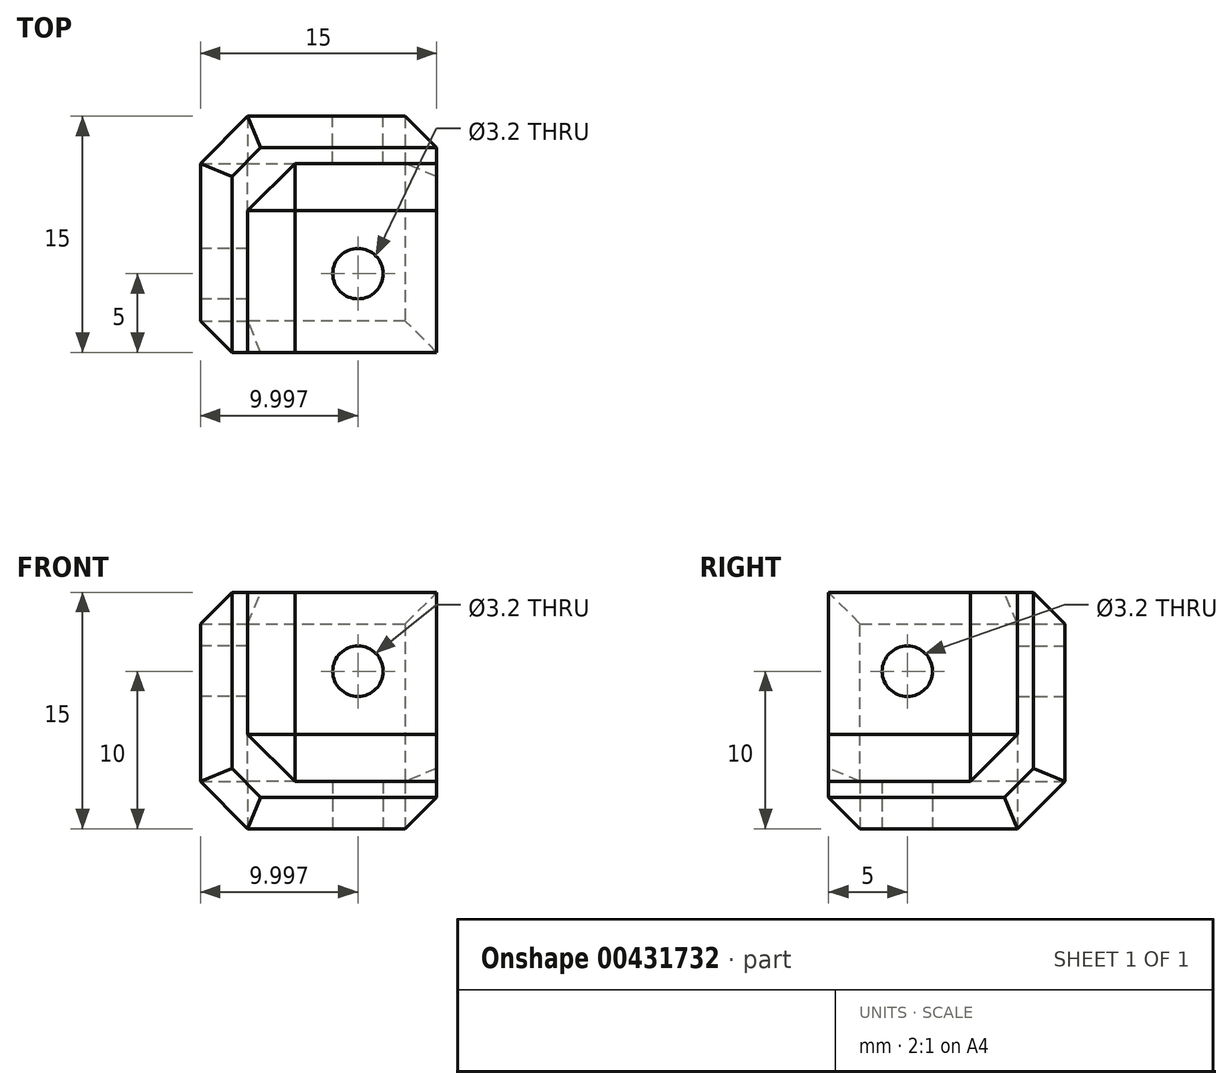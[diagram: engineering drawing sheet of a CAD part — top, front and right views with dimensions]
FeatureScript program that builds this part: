
annotation { "Feature Type Name" : "Feature", "Feature Type Description" : "" }
export const myFeature = defineFeature(function(context is Context, id is Id, definition is map)
    precondition{}
    {
        {
            var Q0;
            Q0=qCreatedBy(makeId("Top.planeOp"),FACE);
            var sketch = newSketch(context, id + "F0", { "sketchPlane" : qUnion([Q0])});
            skLineSegment(sketch, "E0.bottom", {"start": v(-55.5, 0.14) * mm, "end": v(-40.5, 0.14) * mm});
            skLineSegment(sketch, "E0.top", {"start": v(-55.5, -14.86) * mm, "end": v(-40.5, -14.86) * mm});
            skLineSegment(sketch, "E0.left", {"start": v(-55.5, 0.14) * mm, "end": v(-55.5, -14.86) * mm});
            skLineSegment(sketch, "E0.right", {"start": v(-40.5, 0.14) * mm, "end": v(-40.5, -14.86) * mm});
            skLineSegment(sketch, "E1", {"start": v(-52.5, -14.86) * mm, "end": v(-52.5, -2.86) * mm});
            skLineSegment(sketch, "E2", {"start": v(-52.5, -2.86) * mm, "end": v(-40.5, -2.86) * mm});
            skCircle(sketch, "E3", {"center": v(-45.5, -9.86) * mm, "radius": 1.6 * mm});
            skSolve(sketch);
        }
        {
            var Q0;
            {var subQ1=sQuery(id+"F0.wireOp",EDGE,"E0.bottom");Q0=makeQuery(id+"F0.imprint","IMPRINT",FACE,{"disambiguationData":[TD([[makeQuery(id+"F0.imprint","IMPRINT",EDGE,{"derivedFrom":subQ1}),-1.0]])]});}
            var Q1;
            {var subQ3=sQuery(id+"F0.wireOp",EDGE,"E1");Q1=makeQuery(id+"F0.imprint","IMPRINT",FACE,{"disambiguationData":[TD([[makeQuery(id+"F0.imprint","IMPRINT",EDGE,{"derivedFrom":subQ3}),-1.0]])]});}
            extrude(context, id + "F1", {"entities" : qUnion([Q0, Q1]), "depth" : 3 * mm});
        }
        {
            var Q0;
            {var subQ1=sQuery(id+"F0.wireOp",EDGE,"E0.bottom");Q0=makeQuery(id+"F0.imprint","IMPRINT",FACE,{"disambiguationData":[TD([[makeQuery(id+"F0.imprint","IMPRINT",EDGE,{"derivedFrom":subQ1}),-1.0]])]});}
            extrude(context, id + "F2", {"entities" : qUnion([Q0]), "operationType" : NewBodyOperationType.ADD, "depth" : 15 * mm});
        }
        {
            var Q0;
            {var subQ0=sQuery(id+"F0.wireOp",EDGE,"E0.bottom");Q0=makeQuery(id+"F2.boolean.opBoolean","MERGE",FACE,{"derivedFrom":[makeQuery(id+"F1.opExtrude","SWEPT_FACE",FACE,{"disambiguationData":[OSD([subQ0])]}),makeQuery(id+"F2.opExtrude","SWEPT_FACE",FACE,{"disambiguationData":[OSD([subQ0])]})]});}
            var sketch = newSketch(context, id + "F3", { "sketchPlane" : qUnion([Q0])});
            skCircle(sketch, "E4", {"center": v(45.5, 10) * mm, "radius": 1.6 * mm});
            skSolve(sketch);
        }
        {
            var Q0;
            Q0=qSketchRegion(id+"F3",true);
            extrude(context, id + "F4", {"entities" : qUnion([Q0]), "operationType" : NewBodyOperationType.REMOVE, "oppositeDirection" : true, "depth" : 25 * mm});
        }
        {
            var Q0;
            {var subQ0=sQuery(id+"F0.wireOp",EDGE,"E0.left");Q0=makeQuery(id+"F2.boolean.opBoolean","MERGE",FACE,{"derivedFrom":[makeQuery(id+"F1.opExtrude","SWEPT_FACE",FACE,{"disambiguationData":[OSD([subQ0])]}),makeQuery(id+"F2.opExtrude","SWEPT_FACE",FACE,{"disambiguationData":[OSD([subQ0])]})]});}
            var sketch = newSketch(context, id + "F5", { "sketchPlane" : qUnion([Q0])});
            skCircle(sketch, "E5", {"center": v(9.86, 10) * mm, "radius": 1.6 * mm});
            skSolve(sketch);
        }
        {
            var Q0;
            Q0=qSketchRegion(id+"F5",true);
            extrude(context, id + "F6", {"entities" : qUnion([Q0]), "operationType" : NewBodyOperationType.REMOVE, "oppositeDirection" : true, "depth" : 25 * mm});
        }
        {
            var Q0;
            Q0=makeQuery(id+"F2.opExtrude","CAP_VERTEX",VERTEX,{"disambiguationData":[OSD([sQuery(id+"F0.wireOp",EDGE,"E0.top"),sQuery(id+"F0.wireOp",EDGE,"E1")])],"isStart":false});
            var Q1;
            Q1=makeQuery(id+"F2.opExtrude","CAP_VERTEX",VERTEX,{"disambiguationData":[OSD([sQuery(id+"F0.wireOp",EDGE,"E0.right"),sQuery(id+"F0.wireOp",EDGE,"E2")])],"isStart":false});
            var Q2;
            Q2=makeQuery(id+"F1.opExtrude","CAP_VERTEX",VERTEX,{"disambiguationData":[OSD([sQuery(id+"F0.wireOp",EDGE,"E0.top"),sQuery(id+"F0.wireOp",EDGE,"E0.right")])],"isStart":false});
            cPlane(context, id + "F7", {"entities" : qUnion([Q0, Q1, Q2]), "cplaneType" : CPlaneType.THREE_POINT, "offset" : 25 * mm, "width" : 150 * mm, "height" : 150 * mm});
        }
        {
            var Q0;
            Q0=qCreatedBy(id+"F7.planeOp",FACE);
            var sketch = newSketch(context, id + "F8", { "sketchPlane" : qUnion([Q0])});
            skLineSegment(sketch, "E6", {"start": v(-30.2, 50.45) * mm, "end": v(-13.73, 49.44) * mm});
            skLineSegment(sketch, "E7", {"start": v(-13.73, 49.44) * mm, "end": v(-6.86, 39.33) * mm});
            skLineSegment(sketch, "E8", {"start": v(-6.86, 39.33) * mm, "end": v(-16.3, 24.65) * mm});
            skLineSegment(sketch, "E9", {"start": v(-16.3, 24.65) * mm, "end": v(-31.74, 25.37) * mm});
            skLineSegment(sketch, "E10", {"start": v(-31.74, 25.37) * mm, "end": v(-37.56, 38.88) * mm});
            skLineSegment(sketch, "E11", {"start": v(-37.56, 38.88) * mm, "end": v(-30.2, 50.45) * mm});
            skSolve(sketch);
        }
        {
            var Q0;
            Q0=qSketchRegion(id+"F8",true);
            extrude(context, id + "F9", {"entities" : qUnion([Q0]), "operationType" : NewBodyOperationType.REMOVE, "oppositeDirection" : true, "depth" : 3 * mm});
        }
        {
            var Q0;
            Q0=makeQuery(id+"F1.opExtrude","CAP_EDGE",EDGE,{"disambiguationData":[OSD([sQuery(id+"F0.wireOp",EDGE,"E0.left")])],"isStart":true});
            var Q1;
            Q1=makeQuery(id+"F1.opExtrude","CAP_EDGE",EDGE,{"disambiguationData":[OSD([sQuery(id+"F0.wireOp",EDGE,"E0.bottom")])],"isStart":true});
            var Q2;
            {var subQ0=sQuery(id+"F0.wireOp",EDGE,"E0.left");var subQ1=sQuery(id+"F0.wireOp",EDGE,"E0.bottom");Q2=makeQuery(id+"F2.boolean.opBoolean","MERGE",EDGE,{"derivedFrom":[makeQuery(id+"F1.opExtrude","SWEPT_EDGE",EDGE,{"disambiguationData":[OSD([subQ1,subQ0])]}),makeQuery(id+"F2.opExtrude","SWEPT_EDGE",EDGE,{"disambiguationData":[OSD([subQ1,subQ0])]})]});}
            var Q3;
            Q3=makeQuery(id+"F2.boolean.opBoolean","INTERSECT",EDGE,{"derivedFrom":[makeQuery(id+"F1.opExtrude","CAP_FACE",FACE,{"disambiguationData":[OSD([sQuery(id+"F0.wireOp",EDGE,"E0.bottom"),sQuery(id+"F0.wireOp",EDGE,"E0.top"),sQuery(id+"F0.wireOp",EDGE,"E0.left"),sQuery(id+"F0.wireOp",EDGE,"E0.right"),sQuery(id+"F0.wireOp",EDGE,"E3")])],"isStart":false}),makeQuery(id+"F2.opExtrude","SWEPT_FACE",FACE,{"disambiguationData":[OSD([sQuery(id+"F0.wireOp",EDGE,"E1")])]})]});
            var Q4;
            Q4=makeQuery(id+"F2.boolean.opBoolean","INTERSECT",EDGE,{"derivedFrom":[makeQuery(id+"F1.opExtrude","CAP_FACE",FACE,{"disambiguationData":[OSD([sQuery(id+"F0.wireOp",EDGE,"E0.bottom"),sQuery(id+"F0.wireOp",EDGE,"E0.top"),sQuery(id+"F0.wireOp",EDGE,"E0.left"),sQuery(id+"F0.wireOp",EDGE,"E0.right"),sQuery(id+"F0.wireOp",EDGE,"E3")])],"isStart":false}),makeQuery(id+"F2.opExtrude","SWEPT_FACE",FACE,{"disambiguationData":[OSD([sQuery(id+"F0.wireOp",EDGE,"E2")])]})]});
            var Q5;
            Q5=makeQuery(id+"F2.opExtrude","SWEPT_EDGE",EDGE,{"disambiguationData":[OSD([sQuery(id+"F0.wireOp",EDGE,"E1"),sQuery(id+"F0.wireOp",EDGE,"E2")])]});
            chamfer(context, id + "F10", {"entities" : qUnion([Q0, Q1, Q2, Q3, Q4, Q5]), "width" : 3 * mm, "tangentPropagation" : true});
        }
        {
            var Q0;
            {var subQ0=sQuery(id+"F0.wireOp",EDGE,"E0.right");var subQ1=sQuery(id+"F0.wireOp",EDGE,"E0.bottom");Q0=makeQuery(id+"F2.boolean.opBoolean","MERGE",EDGE,{"derivedFrom":[makeQuery(id+"F1.opExtrude","SWEPT_EDGE",EDGE,{"disambiguationData":[OSD([subQ1,subQ0])]}),makeQuery(id+"F2.opExtrude","SWEPT_EDGE",EDGE,{"disambiguationData":[OSD([subQ1,subQ0])]})]});}
            var Q1;
            Q1=makeQuery(id+"F1.opExtrude","CAP_EDGE",EDGE,{"disambiguationData":[OSD([sQuery(id+"F0.wireOp",EDGE,"E0.right")])],"isStart":true});
            var Q2;
            Q2=makeQuery(id+"F1.opExtrude","CAP_EDGE",EDGE,{"disambiguationData":[OSD([sQuery(id+"F0.wireOp",EDGE,"E0.top")])],"isStart":true});
            var Q3;
            {var subQ0=sQuery(id+"F0.wireOp",EDGE,"E0.left");var subQ1=sQuery(id+"F0.wireOp",EDGE,"E0.top");Q3=makeQuery(id+"F2.boolean.opBoolean","MERGE",EDGE,{"derivedFrom":[makeQuery(id+"F1.opExtrude","SWEPT_EDGE",EDGE,{"disambiguationData":[OSD([subQ1,subQ0])]}),makeQuery(id+"F2.opExtrude","SWEPT_EDGE",EDGE,{"disambiguationData":[OSD([subQ1,subQ0])]})]});}
            var Q4;
            {var subQ0=sQuery(id+"F0.wireOp",EDGE,"E0.top");Q4=makeQuery(id+"F10.opChamfer","BLEND_EDGE",EDGE,{"blendedFrom":[makeQuery(id+"F1.opExtrude","CAP_EDGE",EDGE,{"disambiguationData":[OSD([sQuery(id+"F0.wireOp",EDGE,"E0.left")])],"isStart":true}),makeQuery(id+"F2.boolean.opBoolean","MERGE",FACE,{"derivedFrom":[makeQuery(id+"F1.opExtrude","SWEPT_FACE",FACE,{"disambiguationData":[OSD([subQ0])]}),makeQuery(id+"F2.opExtrude","SWEPT_FACE",FACE,{"disambiguationData":[OSD([subQ0])]})]})],"blendedInto":[makeQuery(id+"F2.boolean.opBoolean","MERGE",FACE,{"derivedFrom":[makeQuery(id+"F1.opExtrude","SWEPT_FACE",FACE,{"disambiguationData":[OSD([subQ0])]}),makeQuery(id+"F2.opExtrude","SWEPT_FACE",FACE,{"disambiguationData":[OSD([subQ0])]})]})]});}
            var Q5;
            {var subQ0=sQuery(id+"F0.wireOp",EDGE,"E0.left");var subQ1=sQuery(id+"F0.wireOp",EDGE,"E0.bottom");Q5=makeQuery(id+"F10.opChamfer","BLEND_EDGE",EDGE,{"blendedFrom":[makeQuery(id+"F2.boolean.opBoolean","MERGE",EDGE,{"derivedFrom":[makeQuery(id+"F1.opExtrude","SWEPT_EDGE",EDGE,{"disambiguationData":[OSD([subQ1,subQ0])]}),makeQuery(id+"F2.opExtrude","SWEPT_EDGE",EDGE,{"disambiguationData":[OSD([subQ1,subQ0])]})]}),makeQuery(id+"F2.opExtrude","CAP_FACE",FACE,{"disambiguationData":[OSD([subQ1,sQuery(id+"F0.wireOp",EDGE,"E0.top"),subQ0,sQuery(id+"F0.wireOp",EDGE,"E0.right"),sQuery(id+"F0.wireOp",EDGE,"E1"),sQuery(id+"F0.wireOp",EDGE,"E2")])],"isStart":false})],"blendedInto":[makeQuery(id+"F2.opExtrude","CAP_FACE",FACE,{"disambiguationData":[OSD([subQ1,sQuery(id+"F0.wireOp",EDGE,"E0.top"),subQ0,sQuery(id+"F0.wireOp",EDGE,"E0.right"),sQuery(id+"F0.wireOp",EDGE,"E1"),sQuery(id+"F0.wireOp",EDGE,"E2")])],"isStart":false})]});}
            var Q6;
            Q6=makeQuery(id+"F2.opExtrude","CAP_EDGE",EDGE,{"disambiguationData":[OSD([sQuery(id+"F0.wireOp",EDGE,"E0.left")])],"isStart":false});
            var Q7;
            Q7=makeQuery(id+"F2.opExtrude","CAP_EDGE",EDGE,{"disambiguationData":[OSD([sQuery(id+"F0.wireOp",EDGE,"E0.bottom")])],"isStart":false});
            var Q8;
            {var subQ0=sQuery(id+"F0.wireOp",EDGE,"E0.right");Q8=makeQuery(id+"F10.opChamfer","BLEND_EDGE",EDGE,{"blendedFrom":[makeQuery(id+"F1.opExtrude","CAP_EDGE",EDGE,{"disambiguationData":[OSD([sQuery(id+"F0.wireOp",EDGE,"E0.bottom")])],"isStart":true}),makeQuery(id+"F2.boolean.opBoolean","MERGE",FACE,{"derivedFrom":[makeQuery(id+"F1.opExtrude","SWEPT_FACE",FACE,{"disambiguationData":[OSD([subQ0])]}),makeQuery(id+"F2.opExtrude","SWEPT_FACE",FACE,{"disambiguationData":[OSD([subQ0])]})]})],"blendedInto":[makeQuery(id+"F2.boolean.opBoolean","MERGE",FACE,{"derivedFrom":[makeQuery(id+"F1.opExtrude","SWEPT_FACE",FACE,{"disambiguationData":[OSD([subQ0])]}),makeQuery(id+"F2.opExtrude","SWEPT_FACE",FACE,{"disambiguationData":[OSD([subQ0])]})]})]});}
            chamfer(context, id + "F11", {"entities" : qUnion([Q0, Q1, Q2, Q3, Q4, Q5, Q6, Q7, Q8]), "width" : 2 * mm, "tangentPropagation" : true});
        }
    });
